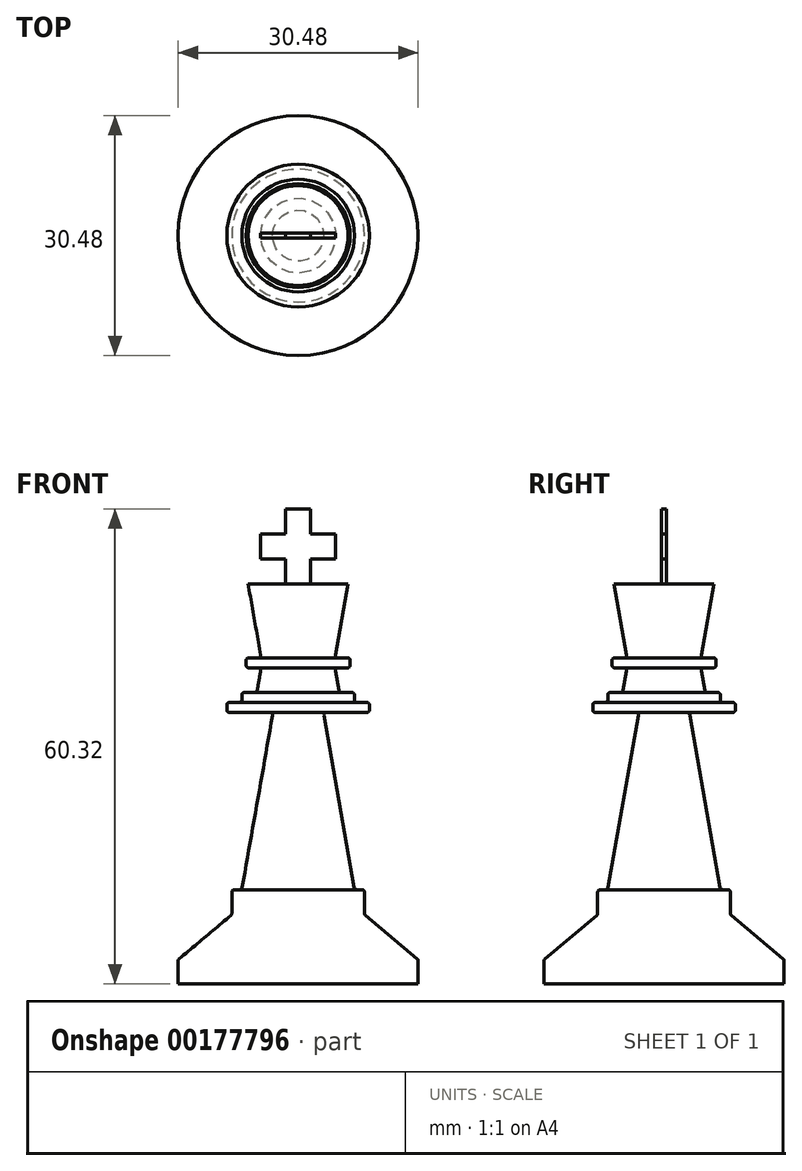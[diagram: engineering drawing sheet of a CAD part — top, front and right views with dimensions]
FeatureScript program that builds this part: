
annotation { "Feature Type Name" : "Feature", "Feature Type Description" : "" }
export const myFeature = defineFeature(function(context is Context, id is Id, definition is map)
    precondition{}
    {
        {
            var Q0;
            Q0=qCreatedBy(makeId("Front.planeOp"),FACE);
            var sketch = newSketch(context, id + "F0", { "sketchPlane" : qUnion([Q0])});
            skLineSegment(sketch, "E0.bottom", {"start": v(0, 0) * mm, "end": v(-15.24, 0) * mm});
            skLineSegment(sketch, "E0.top", {"start": v(0, 50.8) * mm, "end": v(-6.35, 50.8) * mm});
            skLineSegment(sketch, "E0.left", {"start": v(0, 0) * mm, "end": v(0, 50.8) * mm});
            skLineSegment(sketch, "E1", {"start": v(-15.24, 0) * mm, "end": v(-15.24, 2.93) * mm});
            skLineSegment(sketch, "E2", {"start": v(-15.13, 3.18) * mm, "end": v(-8.54, 8.7) * mm});
            skLineSegment(sketch, "E3", {"start": v(-8.43, 8.94) * mm, "end": v(-8.43, 11.65) * mm});
            skLineSegment(sketch, "E4", {"start": v(-8.11, 11.97) * mm, "end": v(-7.43, 11.97) * mm});
            skLineSegment(sketch, "E5", {"start": v(-7.11, 12.23) * mm, "end": v(-3.26, 34.11) * mm});
            skLineSegment(sketch, "E6", {"start": v(-3.57, 34.48) * mm, "end": v(-8.74, 34.48) * mm});
            skLineSegment(sketch, "E7", {"start": v(-9.06, 34.8) * mm, "end": v(-9.06, 35.44) * mm});
            skLineSegment(sketch, "E8", {"start": v(-8.74, 35.75) * mm, "end": v(-7.47, 35.75) * mm});
            skLineSegment(sketch, "E9", {"start": v(-7.15, 36.07) * mm, "end": v(-7.15, 36.7) * mm});
            skLineSegment(sketch, "E10", {"start": v(-6.83, 37.02) * mm, "end": v(-5.51, 37.02) * mm});
            skLineSegment(sketch, "E11", {"start": v(-5.2, 37.29) * mm, "end": v(-4.76, 39.78) * mm});
            skLineSegment(sketch, "E12", {"start": v(-5.07, 40.15) * mm, "end": v(-6.28, 40.15) * mm});
            skLineSegment(sketch, "E13", {"start": v(-6.6, 40.47) * mm, "end": v(-6.6, 41.1) * mm});
            skLineSegment(sketch, "E14", {"start": v(-6.28, 41.42) * mm, "end": v(-5.07, 41.42) * mm});
            skLineSegment(sketch, "E15", {"start": v(-4.76, 41.8) * mm, "end": v(-6.35, 50.8) * mm});
            skPoint(sketch, "E16.visualSharp", {"position": v(-15.24, 3.08) * mm});
            skArc(sketch, "E16.filletArc", {"start": v(-15.13, 3.18) * mm, "mid": v(-15.21, 3.07) * mm, "end": v(-15.24, 2.93) * mm});
            skPoint(sketch, "E17.visualSharp", {"position": v(-8.43, 8.8) * mm});
            skArc(sketch, "E17.filletArc", {"start": v(-8.54, 8.7) * mm, "mid": v(-8.46, 8.8) * mm, "end": v(-8.43, 8.94) * mm});
            skPoint(sketch, "E18.visualSharp", {"position": v(-3.2, 34.48) * mm});
            skArc(sketch, "E18.filletArc", {"start": v(-3.26, 34.11) * mm, "mid": v(-3.33, 34.37) * mm, "end": v(-3.57, 34.48) * mm});
            skPoint(sketch, "E19.visualSharp", {"position": v(-8.43, 11.97) * mm});
            skArc(sketch, "E19.filletArc", {"start": v(-8.11, 11.97) * mm, "mid": v(-8.34, 11.88) * mm, "end": v(-8.43, 11.65) * mm});
            skPoint(sketch, "E20.visualSharp", {"position": v(-7.16, 11.97) * mm});
            skArc(sketch, "E20.filletArc", {"start": v(-7.43, 11.97) * mm, "mid": v(-7.22, 12.04) * mm, "end": v(-7.11, 12.23) * mm});
            skPoint(sketch, "E21.visualSharp", {"position": v(-9.06, 34.48) * mm});
            skArc(sketch, "E21.filletArc", {"start": v(-9.06, 34.8) * mm, "mid": v(-8.96, 34.58) * mm, "end": v(-8.74, 34.48) * mm});
            skPoint(sketch, "E22.visualSharp", {"position": v(-9.06, 35.75) * mm});
            skArc(sketch, "E22.filletArc", {"start": v(-8.74, 35.75) * mm, "mid": v(-8.96, 35.66) * mm, "end": v(-9.06, 35.44) * mm});
            skPoint(sketch, "E23.visualSharp", {"position": v(-7.15, 35.75) * mm});
            skArc(sketch, "E23.filletArc", {"start": v(-7.47, 35.75) * mm, "mid": v(-7.25, 35.85) * mm, "end": v(-7.15, 36.07) * mm});
            skPoint(sketch, "E24.visualSharp", {"position": v(-7.15, 37.02) * mm});
            skArc(sketch, "E24.filletArc", {"start": v(-6.83, 37.02) * mm, "mid": v(-7.06, 36.93) * mm, "end": v(-7.15, 36.7) * mm});
            skPoint(sketch, "E25.visualSharp", {"position": v(-5.25, 37.02) * mm});
            skArc(sketch, "E25.filletArc", {"start": v(-5.51, 37.02) * mm, "mid": v(-5.3, 37.1) * mm, "end": v(-5.2, 37.29) * mm});
            skPoint(sketch, "E26.visualSharp", {"position": v(-4.7, 40.15) * mm});
            skArc(sketch, "E26.filletArc", {"start": v(-4.76, 39.78) * mm, "mid": v(-4.83, 40.04) * mm, "end": v(-5.07, 40.15) * mm});
            skPoint(sketch, "E27.visualSharp", {"position": v(-6.6, 40.15) * mm});
            skArc(sketch, "E27.filletArc", {"start": v(-6.6, 40.47) * mm, "mid": v(-6.5, 40.24) * mm, "end": v(-6.28, 40.15) * mm});
            skPoint(sketch, "E28.visualSharp", {"position": v(-6.6, 41.42) * mm});
            skArc(sketch, "E28.filletArc", {"start": v(-6.28, 41.42) * mm, "mid": v(-6.5, 41.33) * mm, "end": v(-6.6, 41.1) * mm});
            skPoint(sketch, "E29.visualSharp", {"position": v(-4.7, 41.42) * mm});
            skArc(sketch, "E29.filletArc", {"start": v(-5.07, 41.42) * mm, "mid": v(-4.83, 41.53) * mm, "end": v(-4.76, 41.8) * mm});
            skSolve(sketch);
        }
        {
            var Q0;
            Q0=qCreatedBy(makeId("Front.planeOp"),FACE);
            var sketch = newSketch(context, id + "F1", { "sketchPlane" : qUnion([Q0])});
            skLineSegment(sketch, "E30", {"start": v(0, 50.8) * mm, "end": v(0, 60.33) * mm, "construction": true});
            skPoint(sketch, "E30.endSnap0", {"position": v(0, 50.8) * mm});
            skLineSegment(sketch, "E31.bottom", {"start": v(1.59, 50.8) * mm, "end": v(-1.59, 50.8) * mm});
            skLineSegment(sketch, "E31.top", {"start": v(1.59, 60.33) * mm, "end": v(-1.59, 60.33) * mm});
            skLineSegment(sketch, "E31.left", {"start": v(1.59, 50.8) * mm, "end": v(1.59, 53.98) * mm});
            skLineSegment(sketch, "E31.right", {"start": v(-1.59, 50.8) * mm, "end": v(-1.59, 53.98) * mm});
            skPoint(sketch, "E31.middle", {"position": v(0, 55.56) * mm});
            skLineSegment(sketch, "E32.bottom", {"start": v(4.76, 57.15) * mm, "end": v(1.59, 57.15) * mm});
            skLineSegment(sketch, "E32.top", {"start": v(4.76, 53.98) * mm, "end": v(1.59, 53.98) * mm});
            skLineSegment(sketch, "E32.left", {"start": v(4.76, 57.15) * mm, "end": v(4.76, 53.98) * mm});
            skLineSegment(sketch, "E32.right", {"start": v(-4.76, 57.15) * mm, "end": v(-4.76, 53.98) * mm});
            skLineSegment(sketch, "E33.trimOffspring", {"start": v(-1.59, 57.15) * mm, "end": v(-4.76, 57.15) * mm});
            skLineSegment(sketch, "E34.trimOffspring", {"start": v(-1.59, 57.15) * mm, "end": v(-1.59, 60.33) * mm});
            skLineSegment(sketch, "E35.trimOffspring", {"start": v(-1.59, 53.98) * mm, "end": v(-4.76, 53.98) * mm});
            skLineSegment(sketch, "E36.trimOffspring", {"start": v(1.59, 57.15) * mm, "end": v(1.59, 60.33) * mm});
            skLineSegment(sketch, "E37.0", {"start": v(0, 50.8) * mm, "end": v(-6.35, 50.8) * mm});
            skSolve(sketch);
        }
        {
            var Q0;
            Q0=makeQuery(id+"F0.imprint","IMPRINT",FACE,{"disambiguationData":[TD([[makeQuery(id+"F0.imprint","IMPRINT",EDGE,{"derivedFrom":sQuery(id+"F0.wireOp",EDGE,"E0.bottom")}),-1.0]])]});
            var Q1;
            Q1=sQuery(id+"F0.wireOp",EDGE,"E0.left");
            revolve(context, id + "F2", {"entities" : qUnion([Q0]), "axis" : qUnion([Q1]), "revolveType" : RevolveType.FULL});
        }
        {
            var Q0;
            {var subQ0=sQuery(id+"F1.wireOp",EDGE,"E31.bottom");Q0=makeQuery(id+"F1.imprint","IMPRINT",FACE,{"disambiguationData":[TD([[makeQuery(id+"F1.imprint","IMPRINT",EDGE,{"derivedFrom":subQ0}),-1.0]])]});}
            extrude(context, id + "F3", {"entities" : qUnion([Q0]), "operationType" : NewBodyOperationType.ADD, "endBound" : BoundingType.SYMMETRIC, "depth" : 0.64 * mm, "hasSecondDirection" : true, "secondDirectionOppositeDirection" : true, "secondDirectionDepth" : 0.32 * mm});
        }
    });
